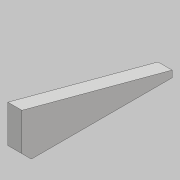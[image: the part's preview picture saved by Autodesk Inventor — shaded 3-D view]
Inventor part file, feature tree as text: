
AUTODESK INVENTOR PART (.ipt)
format: ipt  version: 2018 (Build 220112000, 112)  size: 76,800 bytes
history: native  units: mm
features: other x1, extrude x1, chamfer x1, sketch x1
ambient origin geometry x8: Origin, YZ Plane, XZ Plane, XY Plane, X Axis, Y Axis, Z Axis, Center Point
bodies: Body1 (feature_tree)
feature tree (4):
  other  "實體1"
  extrude  "擠出1"  Depth=160.0mm
  chamfer  "倒角1"  Distance=50.0mm
  sketch  "草圖1"
